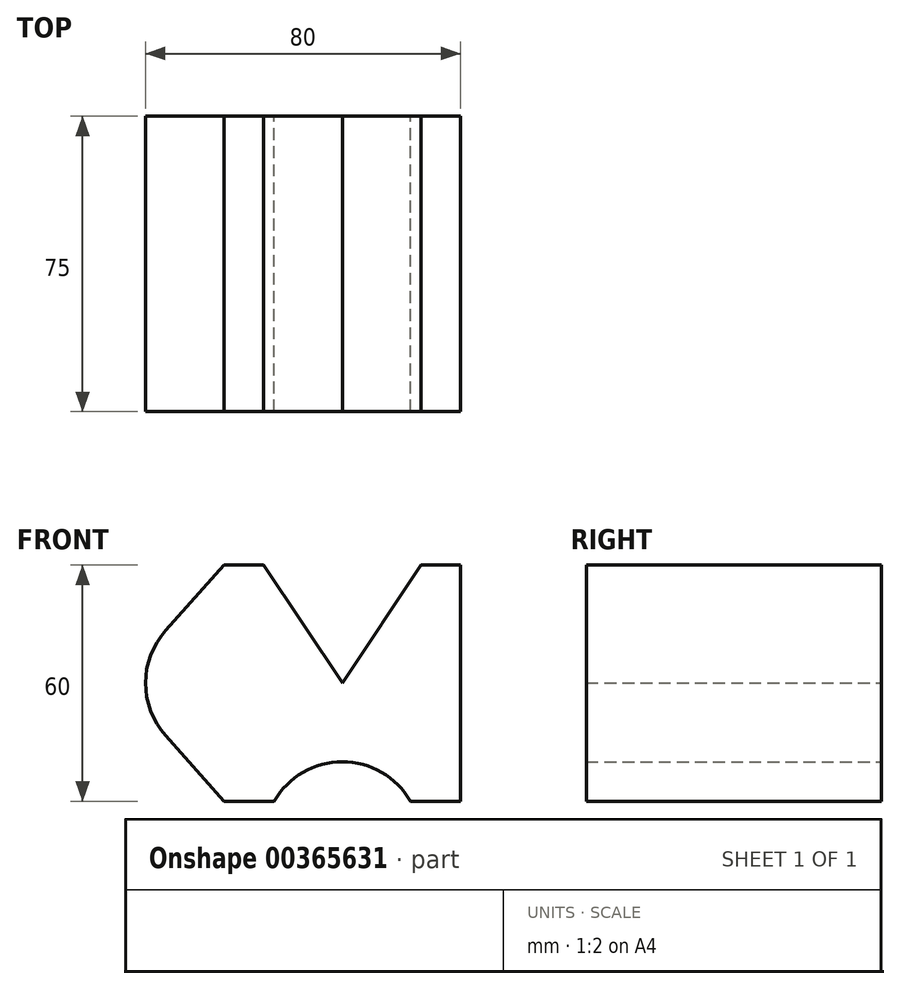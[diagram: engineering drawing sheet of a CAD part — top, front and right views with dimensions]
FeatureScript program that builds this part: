
annotation { "Feature Type Name" : "Feature", "Feature Type Description" : "" }
export const myFeature = defineFeature(function(context is Context, id is Id, definition is map)
    precondition{}
    {
        {
            var Q0;
            Q0=qCreatedBy(makeId("Front.planeOp"),FACE);
            var sketch = newSketch(context, id + "F0", { "sketchPlane" : qUnion([Q0])});
            skLineSegment(sketch, "E0", {"start": v(0, 0) * mm, "end": v(20, 30) * mm});
            skLineSegment(sketch, "E1", {"start": v(20, 30) * mm, "end": v(30, 30) * mm});
            skLineSegment(sketch, "E2", {"start": v(30, 30) * mm, "end": v(30, -30) * mm});
            skLineSegment(sketch, "E3", {"start": v(30, -30) * mm, "end": v(17.32, -30) * mm});
            skArc(sketch, "E4", {"start": v(17.32, -30) * mm, "mid": v(0, -20) * mm, "end": v(-17.32, -30) * mm});
            skLineSegment(sketch, "E5", {"start": v(-17.32, -30) * mm, "end": v(-30, -30) * mm});
            skLineSegment(sketch, "E6", {"start": v(-30, -30) * mm, "end": v(-44.9, -13.33) * mm});
            skArc(sketch, "E7", {"start": v(-44.9, 13.33) * mm, "mid": v(-50, 0) * mm, "end": v(-44.9, -13.33) * mm});
            skLineSegment(sketch, "E8", {"start": v(-44.9, 13.33) * mm, "end": v(-30, 30) * mm});
            skLineSegment(sketch, "E9", {"start": v(-30, 30) * mm, "end": v(-20, 30) * mm});
            skLineSegment(sketch, "E10", {"start": v(-20, 30) * mm, "end": v(0, 0) * mm});
            skLineSegment(sketch, "E11", {"start": v(-30, 30) * mm, "end": v(-30, -30) * mm, "construction": true});
            skSolve(sketch);
        }
        {
            var Q0;
            Q0 = qSketchRegion(id + "F0", true);
            extrude(context, id + "F1", {"entities" : qUnion([Q0]), "depth" : 25 * mm});
        }
        {
            var Q0;
            Q0=makeQuery(id+"F1.opExtrude","CAP_FACE",FACE,{"disambiguationData":[OSD([sQuery(id+"F0.wireOp",EDGE,"E0"),sQuery(id+"F0.wireOp",EDGE,"E1"),sQuery(id+"F0.wireOp",EDGE,"E2"),sQuery(id+"F0.wireOp",EDGE,"E3"),sQuery(id+"F0.wireOp",EDGE,"E4"),sQuery(id+"F0.wireOp",EDGE,"E5"),sQuery(id+"F0.wireOp",EDGE,"E6"),sQuery(id+"F0.wireOp",EDGE,"E7"),sQuery(id+"F0.wireOp",EDGE,"E8"),sQuery(id+"F0.wireOp",EDGE,"E9"),sQuery(id+"F0.wireOp",EDGE,"E10")])],"isStart":false});
            extrude(context, id + "F2", {"entities" : qUnion([Q0]), "operationType" : NewBodyOperationType.ADD, "depth" : 25 * mm});
        }
        {
            var Q0;
            Q0=makeQuery(id+"F2.opExtrude","CAP_FACE",FACE,{"disambiguationData":[OSD([sQuery(id+"F0.wireOp",EDGE,"E0"),sQuery(id+"F0.wireOp",EDGE,"E1"),sQuery(id+"F0.wireOp",EDGE,"E2"),sQuery(id+"F0.wireOp",EDGE,"E3"),sQuery(id+"F0.wireOp",EDGE,"E4"),sQuery(id+"F0.wireOp",EDGE,"E5"),sQuery(id+"F0.wireOp",EDGE,"E6"),sQuery(id+"F0.wireOp",EDGE,"E7"),sQuery(id+"F0.wireOp",EDGE,"E8"),sQuery(id+"F0.wireOp",EDGE,"E9"),sQuery(id+"F0.wireOp",EDGE,"E10")])],"isStart":false});
            var Q1;
            Q1 = qSketchRegion(id + "F0", true);
            extrude(context, id + "F3", {"entities" : qUnion([Q0, Q1]), "operationType" : NewBodyOperationType.ADD, "depth" : 25 * mm});
        }
    });
